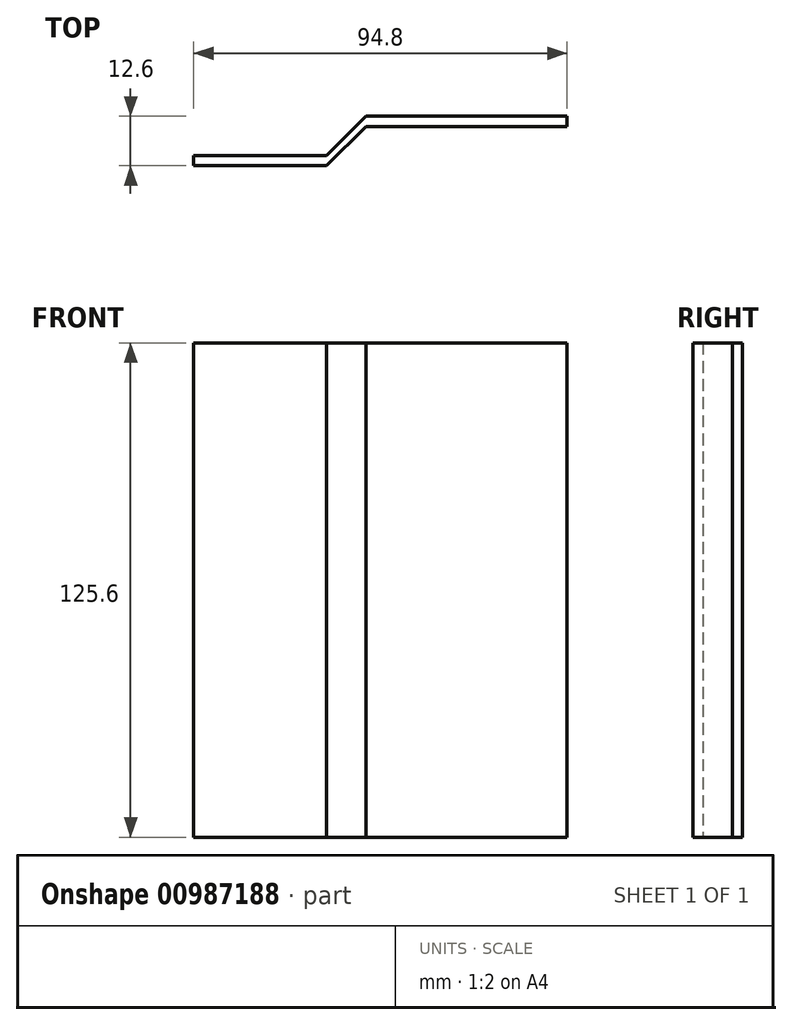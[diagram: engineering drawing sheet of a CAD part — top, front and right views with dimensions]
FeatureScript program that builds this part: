
annotation { "Feature Type Name" : "Feature", "Feature Type Description" : "" }
export const myFeature = defineFeature(function(context is Context, id is Id, definition is map)
    precondition{}
    {
        {
            var Q0;
            Q0=qCreatedBy(makeId("Top.planeOp"),FACE);
            var sketch = newSketch(context, id + "F0", { "sketchPlane" : qUnion([Q0])});
            skLineSegment(sketch, "E0", {"start": v(-49.29, 0) * mm, "end": v(-15.53, 0) * mm});
            skLineSegment(sketch, "E1", {"start": v(-15.53, 0) * mm, "end": v(-5.53, 10) * mm});
            skLineSegment(sketch, "E2", {"start": v(-5.53, 10) * mm, "end": v(45.51, 10) * mm});
            skLineSegment(sketch, "E3", {"start": v(-49.29, 0) * mm, "end": v(-49.29, 2.6) * mm});
            skLineSegment(sketch, "E4", {"start": v(-49.29, 2.6) * mm, "end": v(-15.53, 2.6) * mm});
            skLineSegment(sketch, "E5", {"start": v(-15.53, 2.6) * mm, "end": v(-5.53, 12.6) * mm});
            skLineSegment(sketch, "E6", {"start": v(-5.53, 12.6) * mm, "end": v(45.51, 12.6) * mm});
            skLineSegment(sketch, "E7", {"start": v(45.51, 12.6) * mm, "end": v(45.51, 10) * mm});
            skSolve(sketch);
        }
        {
            var Q0;
            Q0=qSketchRegion(id+"F0",true);
            extrude(context, id + "F1", {"entities" : qUnion([Q0]), "depth" : 125.6 * mm, "offsetDistance" : 25 * mm});
        }
    });
